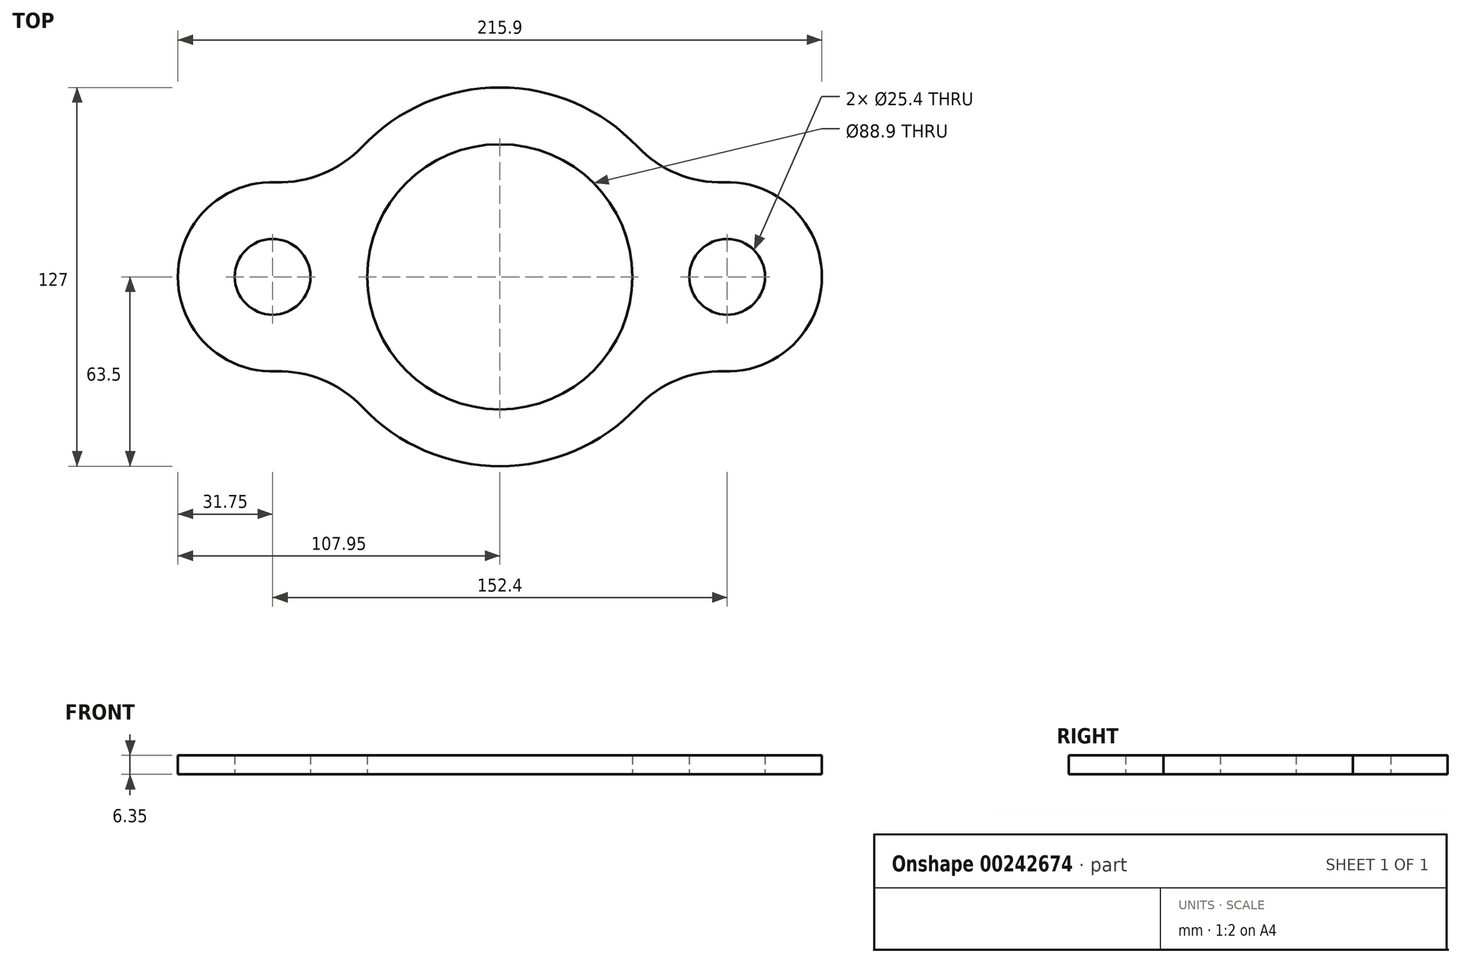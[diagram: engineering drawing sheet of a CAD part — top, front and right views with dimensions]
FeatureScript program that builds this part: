
annotation { "Feature Type Name" : "Feature", "Feature Type Description" : "" }
export const myFeature = defineFeature(function(context is Context, id is Id, definition is map)
    precondition{}
    {
        {
            var Q0;
            Q0=qCreatedBy(makeId("Top.planeOp"),FACE);
            var sketch = newSketch(context, id + "F0", { "sketchPlane" : qUnion([Q0])});
            skCircle(sketch, "E0", {"center": v(0, 0) * mm, "radius": 44.45 * mm});
            skArc(sketch, "E1", {"start": v(-46.14, -43.63) * mm, "mid": v(0, -63.5) * mm, "end": v(46.14, -43.63) * mm});
            skCircle(sketch, "E2", {"center": v(-76.2, 0) * mm, "radius": 12.7 * mm});
            skCircle(sketch, "E3", {"center": v(76.2, 0) * mm, "radius": 12.7 * mm});
            skArc(sketch, "E4", {"start": v(75.12, -31.73) * mm, "mid": v(107.95, 0) * mm, "end": v(75.12, 31.73) * mm});
            skLineSegment(sketch, "E5", {"start": v(-44.45, 0) * mm, "end": v(-44.45, 0) * mm});
            skArc(sketch, "E6.trimOffspring", {"start": v(-75.12, 31.73) * mm, "mid": v(-107.95, 0) * mm, "end": v(-75.12, -31.73) * mm});
            skArc(sketch, "E7.trimOffspring", {"start": v(46.14, 43.63) * mm, "mid": v(0, 63.5) * mm, "end": v(-46.14, 43.63) * mm});
            skPoint(sketch, "E8.visualSharp", {"position": v(-57.94, 25.98) * mm});
            skArc(sketch, "E8.filletArc", {"start": v(-75.12, 31.73) * mm, "mid": v(-59.35, 34.56) * mm, "end": v(-46.14, 43.63) * mm});
            skPoint(sketch, "E9.visualSharp", {"position": v(57.94, 25.98) * mm});
            skArc(sketch, "E9.filletArc", {"start": v(46.14, 43.63) * mm, "mid": v(59.35, 34.56) * mm, "end": v(75.12, 31.73) * mm});
            skPoint(sketch, "E10.visualSharp", {"position": v(57.94, -25.98) * mm});
            skArc(sketch, "E10.filletArc", {"start": v(75.12, -31.73) * mm, "mid": v(59.35, -34.56) * mm, "end": v(46.14, -43.63) * mm});
            skPoint(sketch, "E11.visualSharp", {"position": v(-57.94, -25.98) * mm});
            skArc(sketch, "E11.filletArc", {"start": v(-46.14, -43.63) * mm, "mid": v(-59.35, -34.56) * mm, "end": v(-75.12, -31.73) * mm});
            skSolve(sketch);
        }
        {
            var Q0;
            Q0=makeQuery(id+"F0.imprint","IMPRINT",FACE,{"disambiguationData":[TD([[makeQuery(id+"F0.imprint","IMPRINT",EDGE,{"derivedFrom":sQuery(id+"F0.wireOp",EDGE,"E0")}),-1.0]])]});
            extrude(context, id + "F1", {"entities" : qUnion([Q0]), "depth" : 6.35 * mm});
        }
    });
